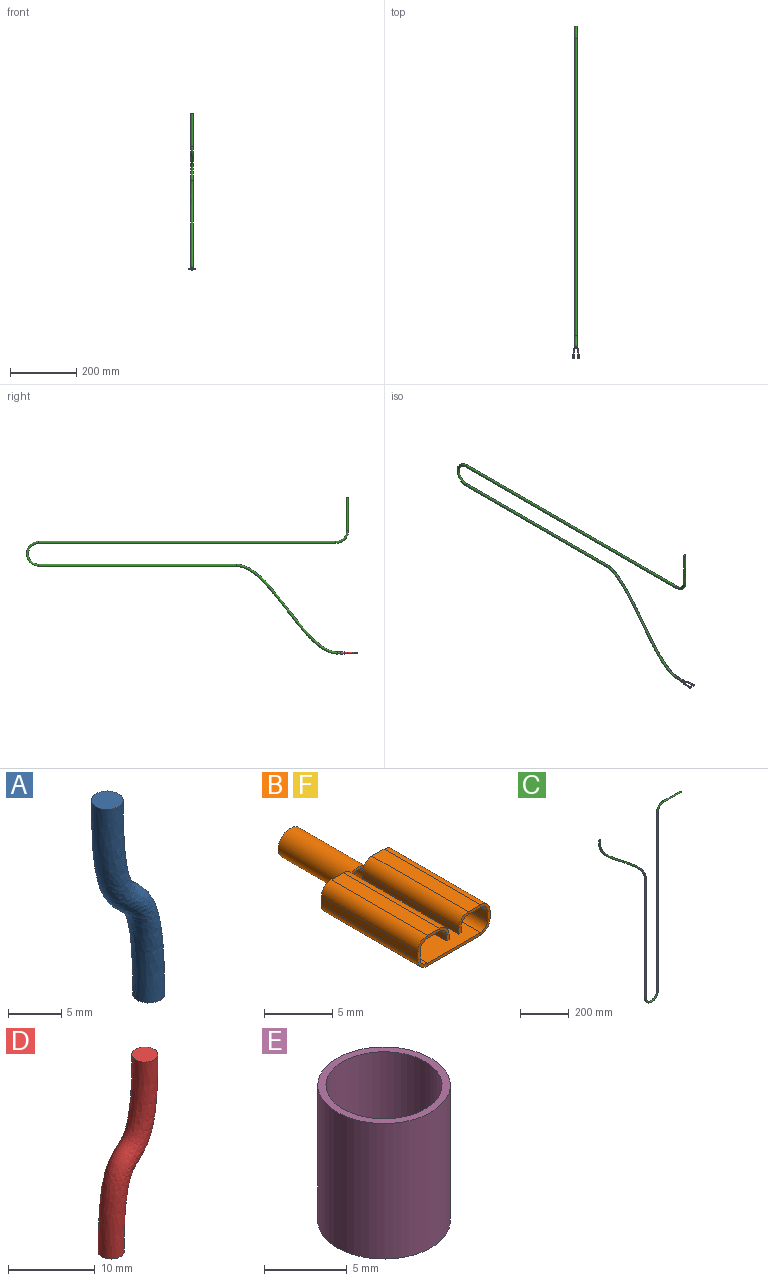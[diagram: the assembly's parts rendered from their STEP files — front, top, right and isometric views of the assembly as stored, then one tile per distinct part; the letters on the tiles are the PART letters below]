
ASSEMBLY  parts=6 mates=4
PART A: 3 faces, bbox 8.5x6x25 mm
  f0: plane 3x3mm, normal (0,0,-1), area 7.1mm2, adj f2
  f1: plane 3x3mm, normal (0,0,1), area 7.1mm2, adj f2
  f2: bspline ~25x8.5mm, area 248.5mm2, adj f0,f1
PART B: 63 faces, bbox 7.5x17x2.8 mm
  f0: plane 2.75x0.25mm, normal (0,1,0), area 0.6mm2, adj f5,f6,f54,f60
  f1: plane 2.75x0.25mm, normal (0,1,0), area 0.6mm2, adj f5,f6,f28,f60
  f2: plane 0.83x0.6mm, normal (0,1,0), area 0.2mm2, adj f11,f22,f23,f60
  f3: plane 0.83x0.6mm, normal (0,1,0), area 0.2mm2, adj f37,f47,f48,f60
  f4: plane 5.5x0.25mm, normal (0,-1,0), area 1.4mm2, adj f5,f6,f29,f53
  f5: plane 10x5.5mm, normal (0,0,-1), area 55mm2, adj f0,f1,f4,f30,f55
  f6: plane 10x5.5mm, normal (0,0,1), area 55mm2, adj f0,f1,f4,f31,f56,f57,f58
  f7: plane 0.75x0.25mm, normal (0,1,0), area 0.2mm2, adj f9,f10,f25,f28
  f8: plane 0.75x0.25mm, normal (0,-1,0), area 0.2mm2, adj f9,f10,f24,f29
  f9: plane 10x0.75mm, normal (-1,0,0), area 7.5mm2, adj f7,f8,f26,f30
  f10: plane 10x0.75mm, normal (1,0,0), area 7.5mm2, adj f7,f8,f27,f31
  f11: plane 1.25x0.25mm, normal (0,1,0), area 0.3mm2, adj f2,f13,f14,f25
  f12: plane 1.25x0.25mm, normal (0,-1,0), area 0.3mm2, adj f13,f14,f20,f24
  f13: plane 10x1.25mm, normal (0,0,1), area 12.5mm2, adj f11,f12,f22,f26
  f14: plane 10x1.25mm, normal (0,0,-1), area 12.5mm2, adj f11,f12,f23,f27
  f15: plane 0.5x0.25mm, normal (0,1,0), area 0.1mm2, adj f17,f18,f19,f21
  f16: plane 0.5x0.25mm, normal (0,-1,0), area 0.1mm2, adj f17,f18,f19,f20
  f17: plane 10x0.25mm, normal (0,0,-1), area 2.5mm2, adj f15,f16,f18,f19
  f18: plane 10x0.5mm, normal (1,0,0), area 5mm2, adj f15,f16,f17,f22
  f19: plane 10x0.5mm, normal (-1,0,0), area 5mm2, adj f15,f16,f17,f23
  f20: plane 1x1mm, normal (0,-1,0), area 0.3mm2, adj f12,f16,f22,f23
  f21: plane 0.33x0.26mm, normal (0,1,0), area 0.1mm2, adj f15,f22,f23,f61
  f22: cylinder r=1mm len=10mm, axis (0,-1,0), area 15.7mm2, adj f2,f13,f18,f20,f21,f59
  f23: cylinder r=0.75mm len=10mm, axis (0,-1,0), area 11.8mm2, adj f2,f14,f19,f20,f21,f57
  f24: plane 1x1mm, normal (0,-1,0), area 0.3mm2, adj f8,f12,f26,f27
  f25: plane 1x1mm, normal (0,1,0), area 0.3mm2, adj f7,f11,f26,f27
  f26: cylinder r=1mm len=10mm, axis (0,-1,0), area 15.7mm2, adj f9,f13,f24,f25
  f27: cylinder r=0.75mm len=10mm, axis (0,-1,0), area 11.8mm2, adj f10,f14,f24,f25
  f28: plane 1x1mm, normal (0,1,0), area 0.3mm2, adj f1,f7,f30,f31
  f29: plane 1x1mm, normal (0,-1,0), area 0.3mm2, adj f4,f8,f30,f31
  f30: cylinder r=1mm len=10mm, axis (0,1,0), area 15.7mm2, adj f5,f9,f28,f29
  f31: cylinder r=0.75mm len=10mm, axis (0,1,0), area 11.8mm2, adj f6,f10,f28,f29
  f32: plane 0.75x0.25mm, normal (0,-1,0), area 0.2mm2, adj f34,f35,f50,f53
  f33: plane 0.75x0.25mm, normal (0,1,0), area 0.2mm2, adj f34,f35,f49,f54
  f34: plane 10x0.75mm, normal (1,0,0), area 7.5mm2, adj f32,f33,f51,f55
  f35: plane 10x0.75mm, normal (-1,0,0), area 7.5mm2, adj f32,f33,f52,f56
  f36: plane 1.25x0.25mm, normal (0,-1,0), area 0.3mm2, adj f38,f39,f46,f50
  f37: plane 1.25x0.25mm, normal (0,1,0), area 0.3mm2, adj f3,f38,f39,f49
  f38: plane 10x1.25mm, normal (0,0,1), area 12.5mm2, adj f36,f37,f47,f51
  f39: plane 10x1.25mm, normal (0,0,-1), area 12.5mm2, adj f36,f37,f48,f52
  f40: plane 0.5x0.25mm, normal (0,-1,0), area 0.1mm2, adj f42,f43,f44,f46
  f41: plane 0.5x0.25mm, normal (0,1,0), area 0.1mm2, adj f42,f43,f44,f45
  f42: plane 10x0.25mm, normal (0,0,-1), area 2.5mm2, adj f40,f41,f43,f44
  f43: plane 10x0.5mm, normal (-1,0,0), area 5mm2, adj f40,f41,f42,f47
  f44: plane 10x0.5mm, normal (1,0,0), area 5mm2, adj f40,f41,f42,f48
  f45: plane 0.33x0.26mm, normal (0,1,0), area 0.1mm2, adj f41,f47,f48,f61
  f46: plane 1x1mm, normal (0,-1,0), area 0.3mm2, adj f36,f40,f47,f48
  f47: cylinder r=1mm len=10mm, axis (0,1,0), area 15.7mm2, adj f3,f38,f43,f45,f46,f59
  f48: cylinder r=0.75mm len=10mm, axis (0,1,0), area 11.8mm2, adj f3,f39,f44,f45,f46,f58
  f49: plane 1x1mm, normal (0,1,0), area 0.3mm2, adj f33,f37,f51,f52
  f50: plane 1x1mm, normal (0,-1,0), area 0.3mm2, adj f32,f36,f51,f52
  f51: cylinder r=1mm len=10mm, axis (0,1,0), area 15.7mm2, adj f34,f38,f49,f50
  f52: cylinder r=0.75mm len=10mm, axis (0,1,0), area 11.8mm2, adj f35,f39,f49,f50
  f53: plane 1x1mm, normal (0,-1,0), area 0.3mm2, adj f4,f32,f55,f56
  f54: plane 1x1mm, normal (0,1,0), area 0.3mm2, adj f0,f33,f55,f56
  f55: cylinder r=1mm len=10mm, axis (0,-1,0), area 15.7mm2, adj f5,f34,f53,f54
  f56: cylinder r=0.75mm len=10mm, axis (0,-1,0), area 11.8mm2, adj f6,f35,f53,f54
  f57: plane 1.9x1.25mm, normal (0,-1,0), area 0.5mm2, adj f6,f23,f60,f61
  f58: plane 1.9x1.25mm, normal (0,-1,0), area 0.5mm2, adj f6,f48,f60,f61
  f59: plane 1.34x0.42mm, normal (0,-1,0), area 0.3mm2, adj f22,f47,f60,f61
  f60: cylinder r=1.25mm len=7mm, axis (0,-1,0), area 55mm2, adj f0,f1,f2,f3,f57,f58,f59,f62
  f61: cylinder r=1mm len=7mm, axis (0,-1,0), area 44mm2, adj f21,f45,f57,f58,f59,f62
  f62: plane 2.5x2.5mm, normal (0,1,0), area 1.8mm2, adj f60,f61
PART C: 9 faces, bbox 473.5x14x983.3 mm
  f0: plane 7x7mm, normal (0,0,1), area 38.5mm2, adj f2
  f1: plane 7x7mm, normal (1,0,0), area 38.5mm2, adj f8
  f2: cylinder r=3.5mm len=20mm, axis (0,0,-1), area 439.8mm2, adj f0,f3
  f3: bspline ~305x272mm, area 9130.3mm2, adj f2,f4
  f4: cylinder r=3.5mm len=600mm, axis (0,0,-1), area 13194.7mm2, adj f3,f5
  f5: torus R=35mm, axis (0,-1,0), area 2418.1mm2, adj f4,f6
  f6: cylinder r=3.5mm len=900mm, axis (0,0,1), area 19792mm2, adj f5,f7
  f7: torus R=35mm, axis (0,1,0), area 1209mm2, adj f6,f8
  f8: cylinder r=3.5mm len=100mm, axis (1,0,0), area 2199.1mm2, adj f1,f7
PART D: 3 faces, bbox 8.5x6x25 mm
  f0: plane 3x3mm, normal (0,0,-1), area 7.1mm2, adj f2
  f1: plane 3x3mm, normal (0,0,1), area 7.1mm2, adj f2
  f2: bspline ~25x8.5mm, area 248.5mm2, adj f0,f1
PART E: 4 faces, bbox 8x8x10 mm
  f0: cylinder r=3.5mm len=10mm, axis (0,0,1), area 219.9mm2, adj f2,f3
  f1: cylinder r=4mm len=10mm, axis (0,0,1), area 251.3mm2, adj f2,f3
  f2: plane 8x8mm, normal (0,0,-1), area 11.8mm2, adj f0,f1
  f3: plane 8x8mm, normal (0,0,1), area 11.8mm2, adj f0,f1
PART F: same geometry as B
PLACE A rot(axis=(0,0.71,-0.71),180deg) t=(-125.6,-159.86,-48.9)mm
PLACE B rot(axis=(0,1,0),180deg) t=(-130.1,-191.86,-47.65)mm
PLACE C rot(axis=(0.58,-0.58,0.58),120deg) t=(-126.1,-159.86,-48.9)mm
PLACE D rot(axis=(0,0.71,-0.71),180deg) t=(-126.6,-159.86,-48.9)mm
PLACE E rot(axis=(0,0.71,-0.71),180deg) t=(-126.1,-159.86,-48.9)mm
PLACE F rot(axis=(0,1,0),180deg) t=(-115.1,-191.86,-47.65)mm
MATE fastened D.f0 <-> E.f3  axis (0,1,0) through (-128.1,-159.86,-48.9)mm
MATE fastened C.f2 <-> E.f0  axis (0,-1,0) through (-126.1,-159.86,-48.9)mm
MATE fastened A.f1 <-> F.f60  axis (0,-1,0) through (-118.6,-184.86,-48.9)mm
MATE fastened D.f1 <-> B.f60  axis (0,-1,0) through (-133.6,-184.86,-48.9)mm
